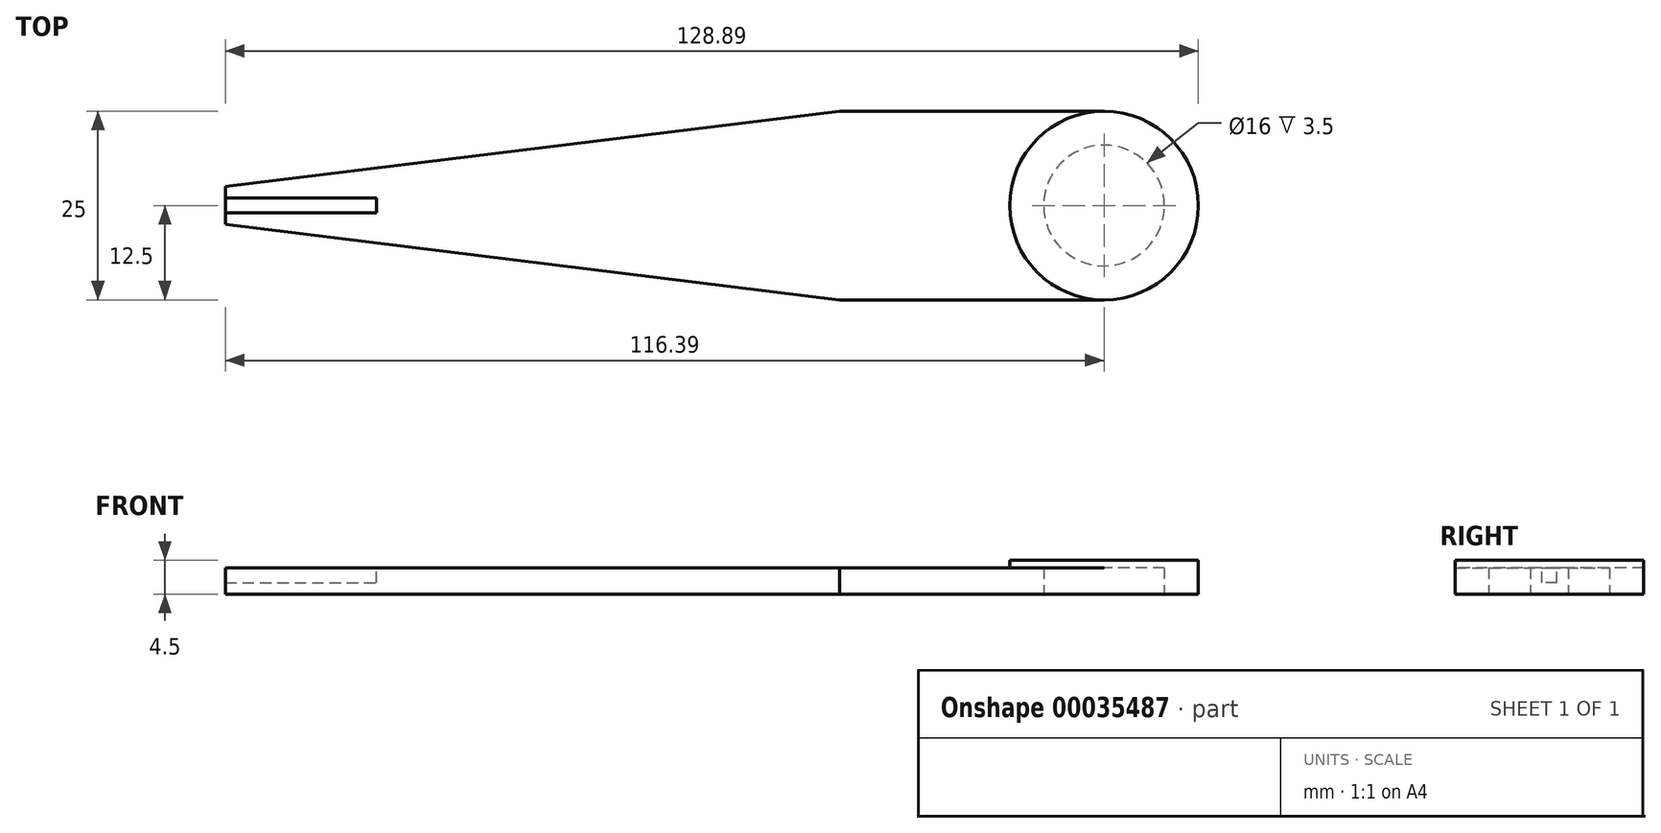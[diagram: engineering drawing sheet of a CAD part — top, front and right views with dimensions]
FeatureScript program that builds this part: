
annotation { "Feature Type Name" : "Feature", "Feature Type Description" : "" }
export const myFeature = defineFeature(function(context is Context, id is Id, definition is map)
    precondition{}
    {
        {
            var Q0;
            Q0=qCreatedBy(makeId("Top.planeOp"),FACE);
            var sketch = newSketch(context, id + "F0", { "sketchPlane" : qUnion([Q0])});
            skCircle(sketch, "E0", {"center": v(0, 0) * mm, "radius": 8 * mm});
            skCircle(sketch, "E1", {"center": v(0, 0) * mm, "radius": 12.5 * mm});
            skLineSegment(sketch, "E2", {"start": v(-35, 12.5) * mm, "end": v(0, 12.5) * mm});
            skLineSegment(sketch, "E3", {"start": v(-35, -12.5) * mm, "end": v(0, -12.5) * mm});
            skLineSegment(sketch, "E4", {"start": v(-35, 12.5) * mm, "end": v(-116.39, 2.5) * mm});
            skLineSegment(sketch, "E5", {"start": v(-35, -12.5) * mm, "end": v(-116.39, -2.5) * mm});
            skLineSegment(sketch, "E6", {"start": v(-116.39, 2.5) * mm, "end": v(-116.39, -2.5) * mm});
            skSolve(sketch);
        }
        {
            var Q0;
            {var subQ1=sQuery(id+"F0.wireOp",EDGE,"E2");Q0=makeQuery(id+"F0.imprint","IMPRINT",FACE,{"disambiguationData":[TD([[makeQuery(id+"F0.imprint","IMPRINT",EDGE,{"derivedFrom":subQ1}),-1.0]])]});}
            var Q1;
            Q1=makeQuery(id+"F0.imprint","IMPRINT",FACE,{"disambiguationData":[TD([[makeQuery(id+"F0.imprint","IMPRINT",EDGE,{"derivedFrom":sQuery(id+"F0.wireOp",EDGE,"E0")}),-1.0]])]});
            extrude(context, id + "F1", {"entities" : qUnion([Q0, Q1]), "depth" : 3.5 * mm});
        }
        {
            var Q0;
            Q0=makeQuery(id+"F1.opExtrude","CAP_FACE",FACE,{"disambiguationData":[OSD([sQuery(id+"F0.wireOp",EDGE,"E0"),sQuery(id+"F0.wireOp",EDGE,"E1"),sQuery(id+"F0.wireOp",EDGE,"E2"),sQuery(id+"F0.wireOp",EDGE,"E3"),sQuery(id+"F0.wireOp",EDGE,"E4"),sQuery(id+"F0.wireOp",EDGE,"E5"),sQuery(id+"F0.wireOp",EDGE,"E6")])],"isStart":false});
            var sketch = newSketch(context, id + "F2", { "sketchPlane" : qUnion([Q0])});
            skPoint(sketch, "E7.center.orphan", {"position": v(0, 0) * mm});
            skCircle(sketch, "E8", {"center": v(0, 0) * mm, "radius": 12.5 * mm});
            skSolve(sketch);
        }
        {
            var Q0;
            Q0 = qSketchRegion(id + "F2", true);
            extrude(context, id + "F3", {"entities" : qUnion([Q0]), "operationType" : NewBodyOperationType.ADD, "depth" : 1 * mm});
        }
        {
            var Q0;
            Q0=makeQuery(id+"F1.opExtrude","CAP_FACE",FACE,{"disambiguationData":[OSD([sQuery(id+"F0.wireOp",EDGE,"E0"),sQuery(id+"F0.wireOp",EDGE,"E1"),sQuery(id+"F0.wireOp",EDGE,"E2"),sQuery(id+"F0.wireOp",EDGE,"E3"),sQuery(id+"F0.wireOp",EDGE,"E4"),sQuery(id+"F0.wireOp",EDGE,"E5"),sQuery(id+"F0.wireOp",EDGE,"E6")])],"isStart":false});
            var sketch = newSketch(context, id + "F4", { "sketchPlane" : qUnion([Q0])});
            skLineSegment(sketch, "E9.bottom", {"start": v(-116.39, 1) * mm, "end": v(-96.39, 1) * mm});
            skLineSegment(sketch, "E9.top", {"start": v(-116.39, -1) * mm, "end": v(-96.39, -1) * mm});
            skLineSegment(sketch, "E9.left", {"start": v(-116.39, 1) * mm, "end": v(-116.39, -1) * mm});
            skLineSegment(sketch, "E9.right", {"start": v(-96.39, 1) * mm, "end": v(-96.39, -1) * mm});
            skSolve(sketch);
        }
        {
            var Q0;
            Q0 = qSketchRegion(id + "F4", true);
            extrude(context, id + "F5", {"entities" : qUnion([Q0]), "operationType" : NewBodyOperationType.REMOVE, "oppositeDirection" : true, "depth" : 2 * mm});
        }
    });
